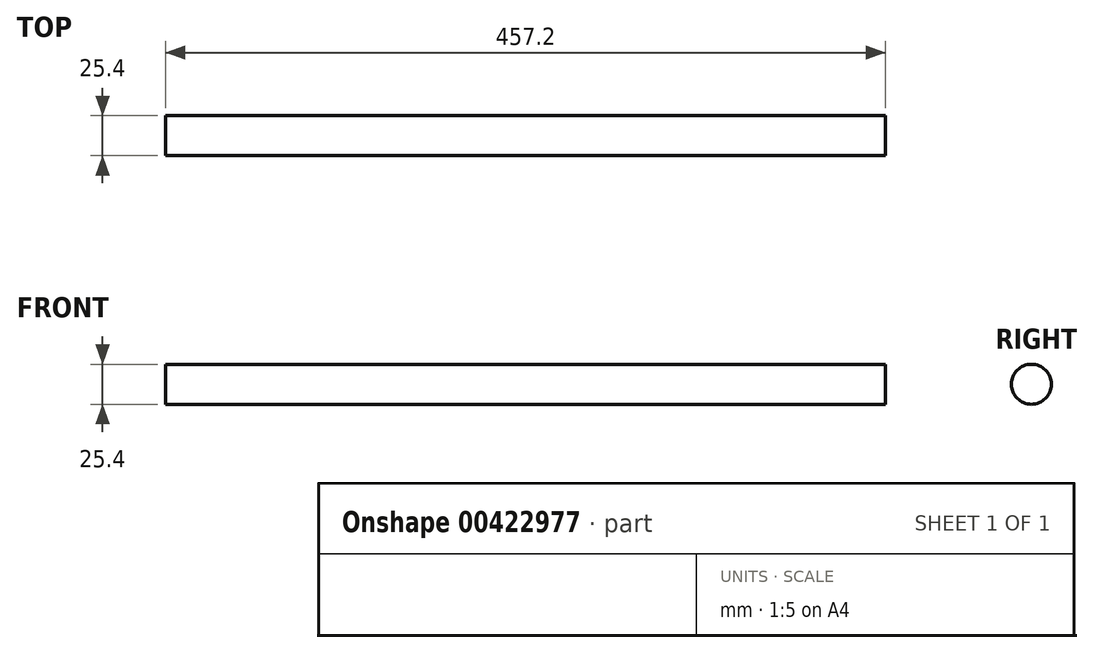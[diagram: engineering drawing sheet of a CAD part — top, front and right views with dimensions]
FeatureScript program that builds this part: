
annotation { "Feature Type Name" : "Feature", "Feature Type Description" : "" }
export const myFeature = defineFeature(function(context is Context, id is Id, definition is map)
    precondition{}
    {
        {
            var Q0;
            Q0=qCreatedBy(makeId("Right.planeOp"),FACE);
            var sketch = newSketch(context, id + "F0", { "sketchPlane" : qUnion([Q0])});
            skCircle(sketch, "E0", {"center": v(0, 0) * mm, "radius": 12.7 * mm});
            skSolve(sketch);
        }
        {
            var Q0;
            Q0=makeQuery(id+"F0.imprint","IMPRINT",FACE,{"disambiguationData":[TD([[makeQuery(id+"F0.imprint","IMPRINT",EDGE,{"derivedFrom":sQuery(id+"F0.wireOp",EDGE,"E0")}),1.0]])]});
            extrude(context, id + "F1", {"entities" : qUnion([Q0]), "depth" : 228.6 * mm, "hasSecondDirection" : true, "secondDirectionOppositeDirection" : true, "secondDirectionDepth" : 228.6 * mm});
        }
    });
